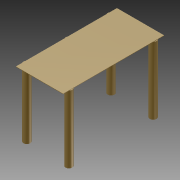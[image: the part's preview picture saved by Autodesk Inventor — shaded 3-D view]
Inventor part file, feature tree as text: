
AUTODESK INVENTOR PART (.ipt)
format: ipt  version: 2011 SP1 (Build 150282100, 282)  size: 91,136 bytes
history: native  units: in
note: dims shown in document units (in); Inventor stores cm internally (conversion verified against a paired STEP export)
features: other x7, extrude x2, sketch x2, pattern_linear x1
ambient origin geometry x8: Origin, YZ Plane, XZ Plane, XY Plane, X Axis, Y Axis, Z Axis, Center Point
bodies: Solid1 (feature_tree)
feature tree (12):
  extrude  "Extrusion1"  Depth=0.16in TaperAngle=0.0deg
  extrude  "Extrusion2"  [1 undecoded]
  pattern_linear  "Rectangular Pattern1"  [2 undecoded]
  other  "to_body_XY"
  other  "to_body_YZ"
  other  "to_body_ZX"
  other  "to_body_X"
  other  "to_body_Y"
  other  "to_body_Z"
  other  "to_body_Center"
  sketch  "Sketch_1"  dims[d0=0.001in d1=0.0in d2=0.16in d3=0.0in]
  sketch  "Sketch_2"  dims[d4=0.7874in d6=0.1in d7=1.1811in d9=0.1in]
note: 3 required parameter values undecoded (feature->parameter linkage not recoverable at this tier; creation-order binding heuristic only, values carry confidence <= 0.55)
